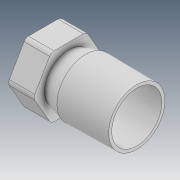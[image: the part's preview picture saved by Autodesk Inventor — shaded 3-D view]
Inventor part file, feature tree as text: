
AUTODESK INVENTOR PART (.ipt)
format: ipt  version: 2020 (Build 240168000, 168)  size: 173,056 bytes
history: native  units: mm
features: sketch x3, extrude x2, chamfer x2, revolve x1, pattern_circular x1, fillet x1
ambient origin geometry x8: Origin, YZ Plane, XZ Plane, XY Plane, X Axis, Y Axis, Z Axis, Center Point
bodies: Solid1 (feature_tree)
feature tree (10):
  revolve  "Revolution1"  [1 undecoded]
  extrude  "Extrusion1"  Depth=11.0mm
  chamfer  "Chamfer1"  Angle=90.0deg  [1 undecoded]
  pattern_circular  "Circular Pattern1"  [2 undecoded]
  chamfer  "Chamfer2"  Distance=1.2mm
  extrude  "Extrusion2"  Depth=10.0mm
  fillet  "Fillet1"  [1 undecoded]
  sketch  "Sketch1"  dims[d2=4.75mm d3=11.25mm]
  sketch  "Sketch2"  dims[d4=20.0mm d5=11.0mm]
  sketch  "Sketch3"  dims[d6=2.0mm d7=90.0deg d8=1.2mm d9=1.2mm d10=10.0mm d11=90.0deg d12=2.443461mm d13=10.0mm d14=0.0mm d15=4.0mm d16=2.0mm d17=45.0deg d18=50.0mm d19=360.0deg d21=0.7mm d22=2.0mm d23=45.0deg d24=30.961694mm d25=8.0mm d26=3.3mm d27=4.6mm d28=6.614426mm d29=10.0mm d30=0.0mm d31=2.0mm d32=24.0mm]
note: 5 required parameter values undecoded (feature->parameter linkage not recoverable at this tier; creation-order binding heuristic only, values carry confidence <= 0.55)